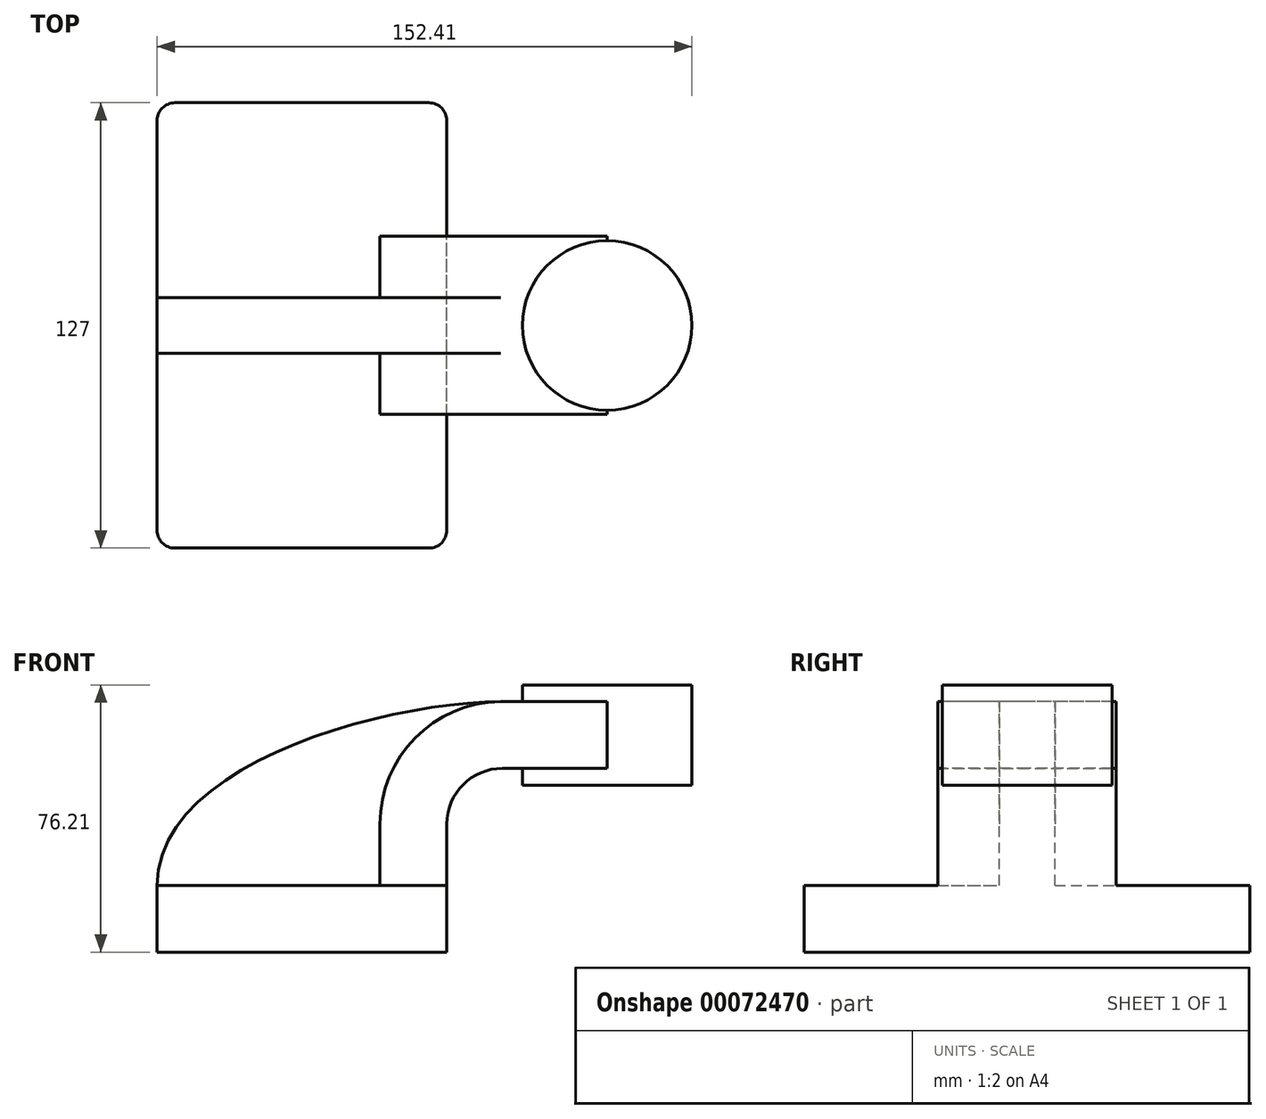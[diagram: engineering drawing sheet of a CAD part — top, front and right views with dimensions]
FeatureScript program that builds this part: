
annotation { "Feature Type Name" : "Feature", "Feature Type Description" : "" }
export const myFeature = defineFeature(function(context is Context, id is Id, definition is map)
    precondition{}
    {
        {
            var Q0;
            Q0=qCreatedBy(makeId("Front.planeOp"),FACE);
            var sketch = newSketch(context, id + "F0", { "sketchPlane" : qUnion([Q0])});
            skLineSegment(sketch, "E0.rect.bottom", {"start": v(-41.28, -9.53) * mm, "end": v(41.28, -9.53) * mm});
            skLineSegment(sketch, "E0.rect.top", {"start": v(-41.28, 9.52) * mm, "end": v(41.28, 9.52) * mm});
            skLineSegment(sketch, "E0.rect.left", {"start": v(-41.28, -9.53) * mm, "end": v(-41.28, 9.52) * mm});
            skLineSegment(sketch, "E0.rect.right", {"start": v(41.28, -9.53) * mm, "end": v(41.28, 9.52) * mm});
            skPoint(sketch, "E0.rect.middle", {"position": v(0, 0) * mm});
            skLineSegment(sketch, "E1.rect.bottom", {"start": v(60.33, 38.1) * mm, "end": v(111.12, 38.1) * mm});
            skLineSegment(sketch, "E1.rect.top", {"start": v(60.33, 66.68) * mm, "end": v(111.12, 66.68) * mm});
            skLineSegment(sketch, "E1.rect.left", {"start": v(60.33, 38.1) * mm, "end": v(60.33, 66.68) * mm});
            skLineSegment(sketch, "E1.rect.right", {"start": v(111.12, 38.1) * mm, "end": v(111.12, 66.68) * mm});
            skPoint(sketch, "E1.rect.middle", {"position": v(85.72, 52.39) * mm});
            skLineSegment(sketch, "E2", {"start": v(41.27, 9.52) * mm, "end": v(41.27, 27) * mm});
            skArc(sketch, "E3", {"start": v(41.27, 27) * mm, "mid": v(45.92, 38.23) * mm, "end": v(57.15, 42.88) * mm});
            skLineSegment(sketch, "E4", {"start": v(57.15, 42.88) * mm, "end": v(86.96, 42.88) * mm});
            skLineSegment(sketch, "E5.0", {"start": v(57.15, 61.93) * mm, "end": v(86.96, 61.93) * mm});
            skArc(sketch, "E5.1", {"start": v(22.23, 27) * mm, "mid": v(32.45, 51.7) * mm, "end": v(57.15, 61.93) * mm});
            skLineSegment(sketch, "E5.2", {"start": v(22.22, 9.52) * mm, "end": v(22.22, 27) * mm});
            skLineSegment(sketch, "E6", {"start": v(86.96, 38.1) * mm, "end": v(86.96, 66.68) * mm});
            skFitSpline(sketch, "E7", {"points": [v(-41.28, 9.53) * mm, v(57.15, 61.93) * mm], "startDerivative": vector(0.87, 104.91) * mm, "endDerivative": vector(100.1, 0.47) * mm});
            skSolve(sketch);
        }
        {
            var Q0;
            {var subQ1=sQuery(id+"F0.wireOp",EDGE,"E2");Q0=makeQuery(id+"F0.imprint","IMPRINT",FACE,{"disambiguationData":[TD([[makeQuery(id+"F0.imprint","IMPRINT",EDGE,{"derivedFrom":subQ1}),1.0]])]});}
            var Q1;
            {var subQ0=sQuery(id+"F0.wireOp",EDGE,"E4");var subQ1=sQuery(id+"F0.wireOp",EDGE,"E1.rect.left");var subQ2=makeQuery(id+"F0.imprint","INTERSECT",VERTEX,{"derivedFrom":[subQ1,subQ0]});Q1=makeQuery(id+"F0.imprint","IMPRINT",FACE,{"disambiguationData":[TD([[makeQuery(id+"F0.imprint","IMPRINT",EDGE,{"disambiguationData":[TD([[subQ2,-1.0]])],"derivedFrom":subQ1}),-1.0]])]});}
            extrude(context, id + "F1", {"entities" : qUnion([Q0, Q1]), "endBound" : BoundingType.SYMMETRIC, "depth" : 50.8 * mm});
        }
        {
            var Q0;
            Q0=makeQuery(id+"F0.imprint","IMPRINT",FACE,{"disambiguationData":[TD([[makeQuery(id+"F0.imprint","IMPRINT",EDGE,{"derivedFrom":sQuery(id+"F0.wireOp",EDGE,"E0.rect.bottom")}),1.0]])]});
            extrude(context, id + "F2", {"entities" : qUnion([Q0]), "operationType" : NewBodyOperationType.ADD, "endBound" : BoundingType.SYMMETRIC, "depth" : 127 * mm});
        }
        {
            var Q0;
            {var subQ3=sQuery(id+"F0.wireOp",EDGE,"E5.2");Q0=makeQuery(id+"F0.imprint","IMPRINT",FACE,{"disambiguationData":[TD([[makeQuery(id+"F0.imprint","IMPRINT",EDGE,{"derivedFrom":subQ3}),1.0]])]});}
            extrude(context, id + "F3", {"entities" : qUnion([Q0]), "operationType" : NewBodyOperationType.ADD, "endBound" : BoundingType.SYMMETRIC, "depth" : 15.88 * mm});
        }
        {
            var Q0;
            Q0=makeQuery(id+"F2.opExtrude","CAP_EDGE",EDGE,{"disambiguationData":[OSD([sQuery(id+"F0.wireOp",EDGE,"E0.rect.left")])],"isStart":true});
            var Q1;
            Q1=makeQuery(id+"F2.opExtrude","CAP_EDGE",EDGE,{"disambiguationData":[OSD([sQuery(id+"F0.wireOp",EDGE,"E0.rect.right")])],"isStart":true});
            var Q2;
            Q2=makeQuery(id+"F2.opExtrude","CAP_EDGE",EDGE,{"disambiguationData":[OSD([sQuery(id+"F0.wireOp",EDGE,"E0.rect.right")])],"isStart":false});
            var Q3;
            Q3=makeQuery(id+"F2.opExtrude","CAP_EDGE",EDGE,{"disambiguationData":[OSD([sQuery(id+"F0.wireOp",EDGE,"E0.rect.left")])],"isStart":false});
            fillet(context, id + "F4", {"entities" : qUnion([Q0, Q1, Q2, Q3]), "radius" : 5.08 * mm, "tangentPropagation" : true, "allowEdgeOverflow" : false});
        }
        {
            var Q0;
            {var subQ0=sQuery(id+"F0.wireOp",EDGE,"E1.rect.right");Q0=makeQuery(id+"F0.imprint","IMPRINT",FACE,{"disambiguationData":[TD([[makeQuery(id+"F0.imprint","IMPRINT",EDGE,{"derivedFrom":subQ0}),1.0]])]});}
            var Q1;
            Q1=sQuery(id+"F0.wireOp",EDGE,"E6");
            revolve(context, id + "F5", {"operationType" : NewBodyOperationType.ADD, "entities" : qUnion([Q0]), "axis" : qUnion([Q1]), "revolveType" : RevolveType.FULL});
        }
    });
